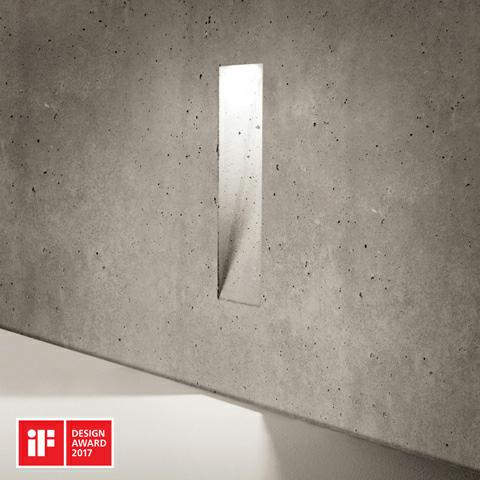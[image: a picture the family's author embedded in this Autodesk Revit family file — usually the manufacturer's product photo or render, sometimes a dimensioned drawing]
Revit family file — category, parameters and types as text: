
# Revit family: SIMES_C.8024W_Ghost
name_source: partatom
category: Lighting Fixtures
revit_build: Autodesk Revit 2016 (Build: 20150714_1515(x64)
units: mm (PartAtom-declared; Revit-internal decimal feet)

## family parameters
Cut with Voids When Loaded = No
Host = Face
Light Source = Yes
OmniClass Number = 23.80.70.14
OmniClass Title = Luminaries for External Lighting
Part Type = Normal
Room Calculation Point = No
Round Connector Dimension = Use Diameter
Shared = No

## types (1)
- SIMES_C.8024W_Ghost
    Approval mark = CE
    Assembly Code = D5020
    Color Filter = 16777215
    Color Rendering Index = CRI 80
    Colour Temperature = 3000
    Control Gear = electronic transformer
    Default Elevation = 1219 mm
    Description = GHOST VERTICAL
Art. C.8024W
MODULES LED COB 3000K  230V CRI 80
Rated luminaire luminous flux: 612lm
Rated input power: 7.6W
Luminaire efficacy: 81lm/W
Electronic ballast 220÷240V 50-60Hz
CE

PRODUCT TYPE
Wall mounted luminaire. IP rating IP 65
MATERIAL CHARACTERISTICS
Ghost is a lighting void that is obtained from a polypropylene housing anchored to the retaining panels before pouring the concrete. Ghost is composed of two elements: the housing and the lighting element. The housing is in polypropylene and it consists of two complementary parts: - A jig , which forms the housing, and is extracted together with the retaining panel after completing the casting and removing the anchor screws; - The housing  that remains embedded inside the casting and houses the lighting element. (The housing is supplied with bolts, locking system and stickers to be applied on the outside of the retaining panels so to secure a perfect alignment for multiple installations of each housing when pouring the concrete). The lighting element in die cast aluminum is anchored to the casing  through proper screws and it remains completely hided into the void. Mechanical resistance IK 06
MAINTENANCE
This product is manufactured on site during the concrete casting of the wall with hand crafted procedures; therefore, small imperfections caused by the low accurance of the casting, subsidence of the concrete surface, actual and future cracks, colour ripples and variations over time, will be deliberately present and they are a feature of the concrete, proving the hand-made manufacturing procedure.
LIGHTING PERFORMANCE
Toughened glass diffuser. LOR -- 
WIRING
Supplied with a pre-wired 6m H05RN-F cable. Isolation: CLASS I . Available colours: Cast cement. Weight: 1.8 Kg Glow Wire test: --
L.E.D circuit included.
GHOST PATENDED, REGISTERED DESIGN
This luminaire contains built-in LED modules with energy class: A, A+, A++. In case of damage or malfunction please contact the manufacturer to receive additional instructions on how to replace and relative spare parts to order. The LED modules cannot be handled in the luminaire by the end user (Regulation UE 874/2012).
LED circuit boards are engineered accordingly to actual Lumen Maintenance regulation (LM80) and Technical Memorandum (TM21) where uniformity and quality of light is 50.000 hours referred to L70  B20 Ta 25°C.Lifecycle refers to LED circuit boards only, all others components of the luminaire are excluded.
    Dimming Lamp Color Temperature Shift = <None>
    Frequency = 50-60Hz
    IFC Classification = Light Fixture
    IK Rating = IK 06
    Lamp = LED
    Lamp Light Flux = 800
    Lamp count = 1
    Last Update = 02/08/2018 10:21:27
    Lifetime = 50000 L70 B20 Ta 25°C
    Light Output Ratio = 100
    Luminous efficacy = 80,5
    Manufacturer = SIMES
    Masterformat 2014 Code = 26 56 00
    Masterformat 2014 Description = Exterior Lighting
    Model = C.8024W
    Mounting Place = Wall
    Mounting Type = Recessed
    NBS Reference Code = 49
    NBS Reference Description = Luminaries And Lamps
    OmniClass Code = 23-35 47 11
    OmniClass Description = Lighting Fixture
    Photometric Web File = C8024W.ies
    Product Group = recessed luminaire
    Product Name = Ghost for cast concrete
    Protection Class = Protection class I
    Protection Degree = IP 65
    System Light Flux = 612
    System Power = 7,59999990463257
    Tilt Angle = 0.00°
    Type Comments = SIMES S.p.A. - All rights reserved
    Type Image = Ghost_verticale.jpg
    UNSPSC Code = 3911
    URL = http://www.simes.it
    Uniclass 1.4 Code = YJ73
    Uniclass 1.4 Description = Luminaries and lamps
    Uniclass 2.0 Code = PR-49
    Uniclass 2.0 Description = Luminaries and lamps
    Uniclass 2015 Code = EF_70_80
    Uniclass 2015 Name = Lighting
    Uniformat II Code = D5020
    Uniformat II Description = Lighting & Branch Wiring
    Voltage = 220÷240V
    Wattage Comments = 7.0W
